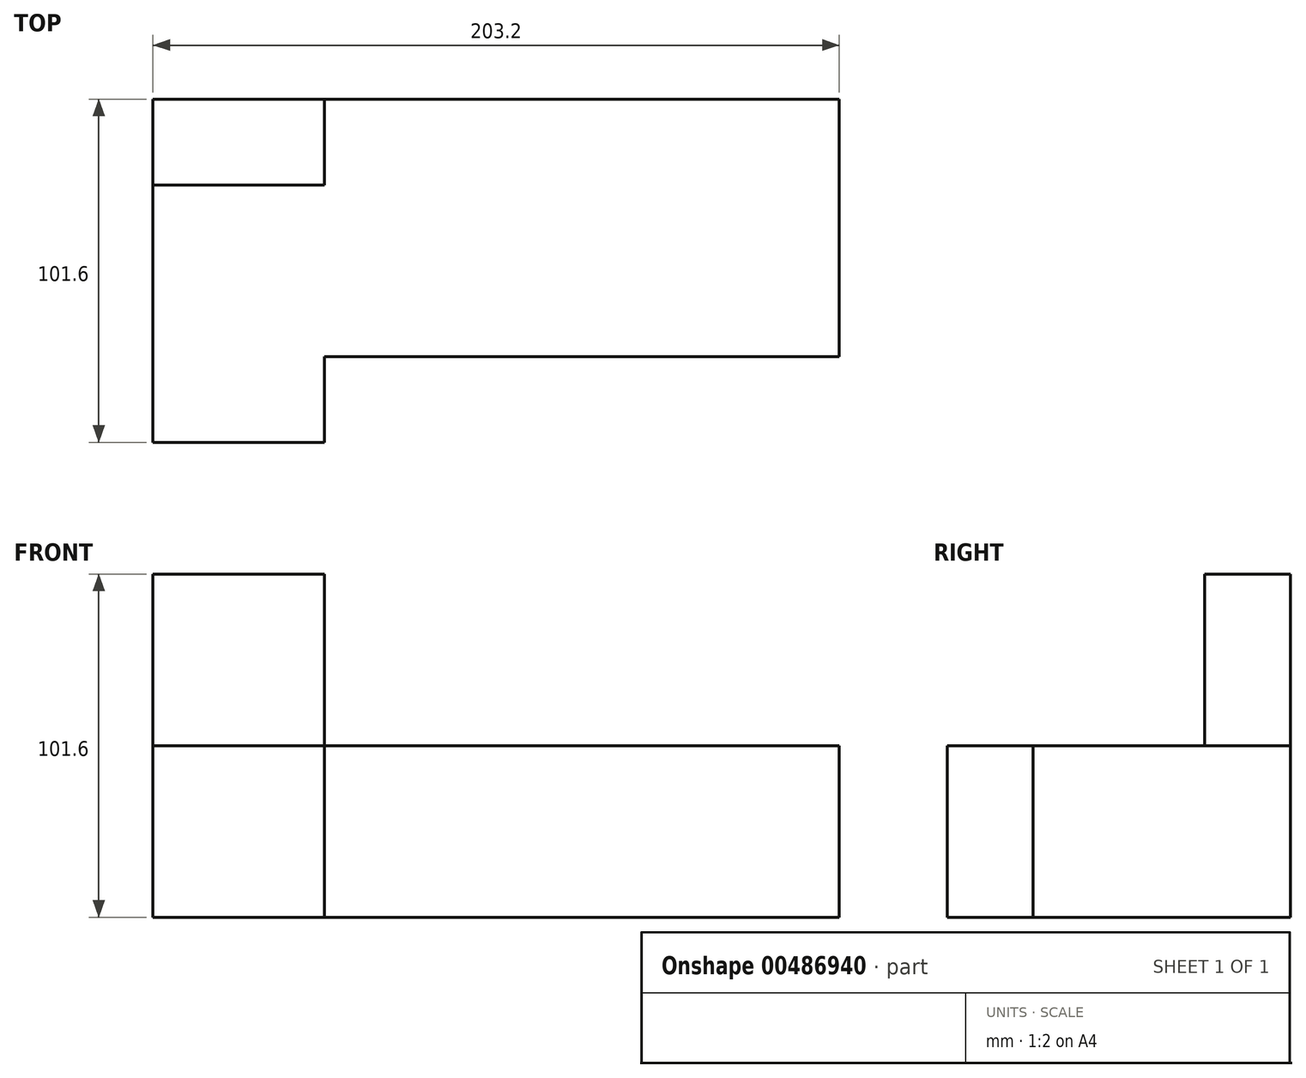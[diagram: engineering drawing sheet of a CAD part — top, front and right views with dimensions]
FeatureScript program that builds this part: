
annotation { "Feature Type Name" : "Feature", "Feature Type Description" : "" }
export const myFeature = defineFeature(function(context is Context, id is Id, definition is map)
    precondition{}
    {
        {
            var Q0;
            Q0=qCreatedBy(makeId("Front.planeOp"),FACE);
            var sketch = newSketch(context, id + "F0", { "sketchPlane" : qUnion([Q0])});
            skLineSegment(sketch, "E0.bottom", {"start": v(-101.6, 50.8) * mm, "end": v(101.6, 50.8) * mm});
            skLineSegment(sketch, "E0.top", {"start": v(-101.6, -50.8) * mm, "end": v(101.6, -50.8) * mm});
            skLineSegment(sketch, "E0.left", {"start": v(-101.6, 50.8) * mm, "end": v(-101.6, -50.8) * mm});
            skLineSegment(sketch, "E0.right", {"start": v(101.6, 50.8) * mm, "end": v(101.6, -50.8) * mm});
            skPoint(sketch, "E0.middle", {"position": v(0, 0) * mm});
            skSolve(sketch);
        }
        {
            var Q0;
            Q0 = qSketchRegion(id + "F0", true);
            extrude(context, id + "F1", {"entities" : qUnion([Q0]), "depth" : 101.6 * mm});
        }
        {
            var Q0;
            Q0=makeQuery(id+"F1.opExtrude","SWEPT_FACE",FACE,{"disambiguationData":[OSD([sQuery(id+"F0.wireOp",EDGE,"E0.bottom")])]});
            var sketch = newSketch(context, id + "F2", { "sketchPlane" : qUnion([Q0])});
            skLineSegment(sketch, "E1", {"start": v(-101.6, -25.4) * mm, "end": v(-50.8, -25.4) * mm});
            skLineSegment(sketch, "E2", {"start": v(-50.8, -25.4) * mm, "end": v(-50.8, 0) * mm});
            skLineSegment(sketch, "E3", {"start": v(-50.8, 0) * mm, "end": v(101.6, 0) * mm});
            skLineSegment(sketch, "E4", {"start": v(101.6, 0) * mm, "end": v(101.6, -101.6) * mm});
            skLineSegment(sketch, "E5", {"start": v(101.6, -101.6) * mm, "end": v(-101.6, -101.6) * mm});
            skLineSegment(sketch, "E6", {"start": v(-101.6, -101.6) * mm, "end": v(-101.6, -25.4) * mm});
            skSolve(sketch);
        }
        {
            var Q0;
            Q0 = qSketchRegion(id + "F2", true);
            extrude(context, id + "F3", {"entities" : qUnion([Q0]), "operationType" : NewBodyOperationType.REMOVE, "oppositeDirection" : true, "depth" : 50.8 * mm});
        }
        {
            var Q0;
            Q0=makeQuery(id+"F3.boolean.opBoolean","COPY",FACE,{"derivedFrom":makeQuery(id+"F3.opExtrude","CAP_FACE",FACE,{"disambiguationData":[OSD([sQuery(id+"F2.wireOp",EDGE,"E1"),sQuery(id+"F2.wireOp",EDGE,"E2"),sQuery(id+"F2.wireOp",EDGE,"E3"),sQuery(id+"F2.wireOp",EDGE,"E4"),sQuery(id+"F2.wireOp",EDGE,"E5"),sQuery(id+"F2.wireOp",EDGE,"E6")])],"isStart":false})});
            var sketch = newSketch(context, id + "F4", { "sketchPlane" : qUnion([Q0])});
            skLineSegment(sketch, "E7.bottom", {"start": v(-50.8, -101.6) * mm, "end": v(101.6, -101.6) * mm});
            skLineSegment(sketch, "E7.top", {"start": v(-50.8, -76.2) * mm, "end": v(101.6, -76.2) * mm});
            skLineSegment(sketch, "E7.left", {"start": v(-50.8, -101.6) * mm, "end": v(-50.8, -76.2) * mm});
            skLineSegment(sketch, "E7.right", {"start": v(101.6, -101.6) * mm, "end": v(101.6, -76.2) * mm});
            skSolve(sketch);
        }
        {
            var Q0;
            Q0 = qSketchRegion(id + "F4", true);
            extrude(context, id + "F5", {"entities" : qUnion([Q0]), "operationType" : NewBodyOperationType.REMOVE, "oppositeDirection" : true, "depth" : 50.8 * mm});
        }
    });
